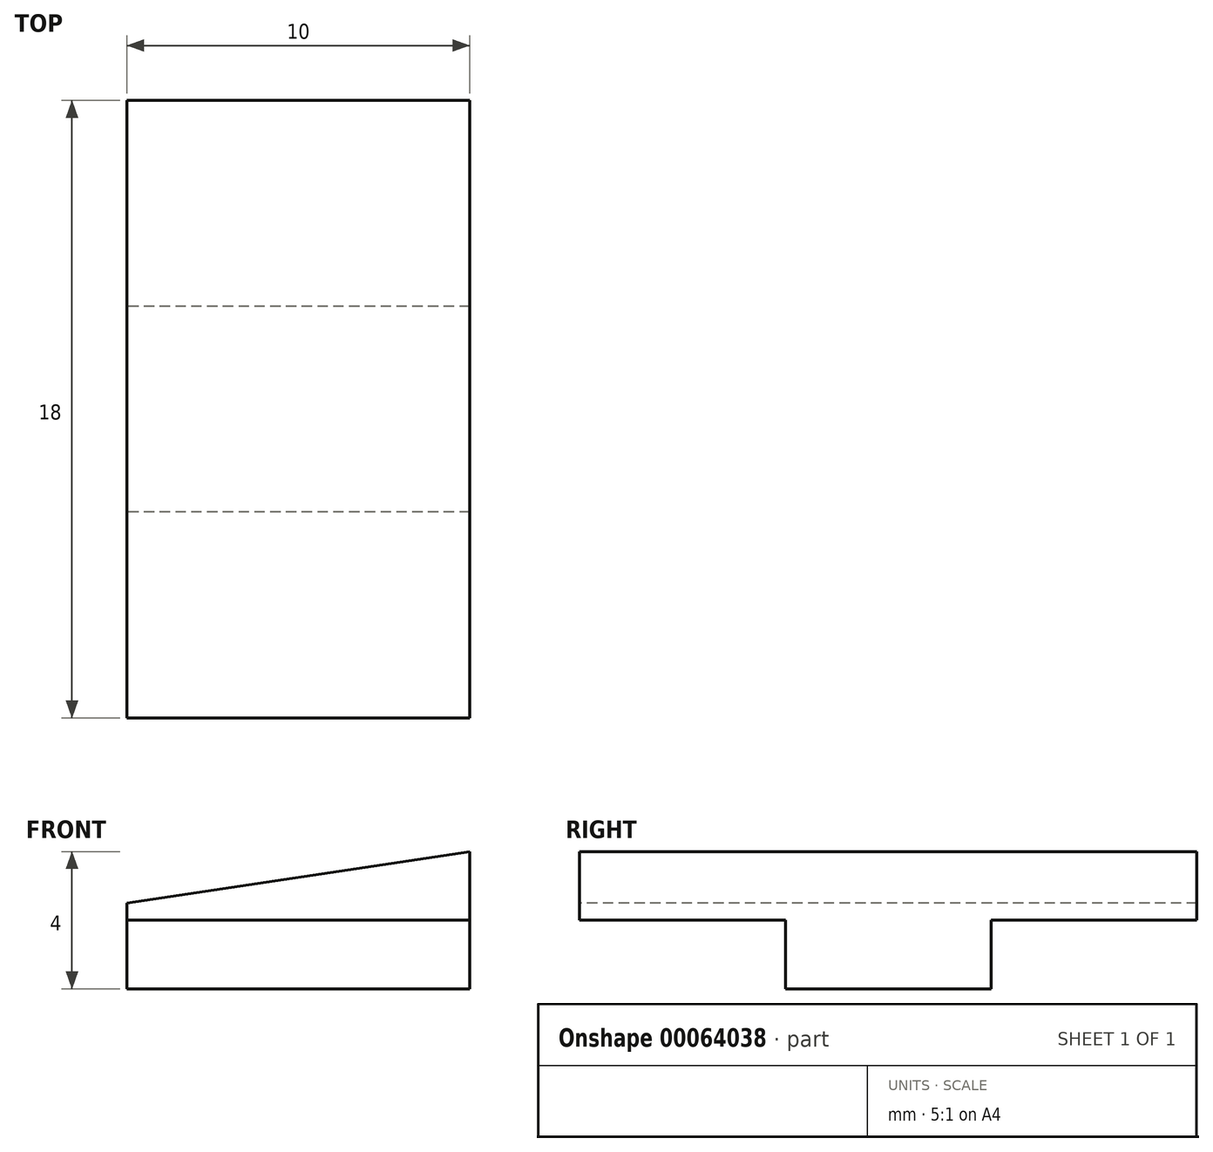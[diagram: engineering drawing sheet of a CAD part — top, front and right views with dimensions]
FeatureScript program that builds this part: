
annotation { "Feature Type Name" : "Feature", "Feature Type Description" : "" }
export const myFeature = defineFeature(function(context is Context, id is Id, definition is map)
    precondition{}
    {
        {
            var Q0;
            Q0=qCreatedBy(makeId("Top.planeOp"),FACE);
            var sketch = newSketch(context, id + "F0", { "sketchPlane" : qUnion([Q0])});
            skLineSegment(sketch, "E0.rect.bottom", {"start": v(5, -9) * mm, "end": v(-5, -9) * mm});
            skLineSegment(sketch, "E0.rect.top", {"start": v(5, 9) * mm, "end": v(-5, 9) * mm});
            skLineSegment(sketch, "E0.rect.left", {"start": v(5, -9) * mm, "end": v(5, 9) * mm});
            skLineSegment(sketch, "E0.rect.right", {"start": v(-5, -9) * mm, "end": v(-5, 9) * mm});
            skPoint(sketch, "E0.rect.middle", {"position": v(0, 0) * mm});
            skSolve(sketch);
        }
        {
            var Q0;
            Q0=makeQuery(id+"F0.imprint","IMPRINT",FACE,{"disambiguationData":[TD([[makeQuery(id+"F0.imprint","IMPRINT",EDGE,{"derivedFrom":sQuery(id+"F0.wireOp",EDGE,"E0.rect.bottom")}),-1.0]])]});
            extrude(context, id + "F1", {"entities" : qUnion([Q0]), "depth" : 4 * mm});
        }
        {
            var Q0;
            Q0=makeQuery(id+"F1.opExtrude","SWEPT_FACE",FACE,{"disambiguationData":[OSD([sQuery(id+"F0.wireOp",EDGE,"E0.rect.bottom")])]});
            var sketch = newSketch(context, id + "F2", { "sketchPlane" : qUnion([Q0])});
            skLineSegment(sketch, "E1", {"start": v(-5, 0.5) * mm, "end": v(5, 2) * mm});
            skLineSegment(sketch, "E2", {"start": v(-5, 0.5) * mm, "end": v(-5, 0) * mm});
            skLineSegment(sketch, "E3", {"start": v(-5, 0) * mm, "end": v(5, 0) * mm});
            skLineSegment(sketch, "E4", {"start": v(5, 0) * mm, "end": v(5, 2) * mm});
            skSolve(sketch);
        }
        {
            var Q0;
            Q0=makeQuery(id+"F2.imprint","IMPRINT",FACE,{"disambiguationData":[TD([[makeQuery(id+"F2.imprint","IMPRINT",EDGE,{"derivedFrom":sQuery(id+"F2.wireOp",EDGE,"E1")}),-1.0]])]});
            extrude(context, id + "F3", {"entities" : qUnion([Q0]), "operationType" : NewBodyOperationType.INTERSECT, "endBound" : BoundingType.THROUGH_ALL, "oppositeDirection" : true, "depth" : 25 * mm});
        }
        {
            var Q0;
            Q0=makeQuery(id+"F1.opExtrude","CAP_FACE",FACE,{"disambiguationData":[OSD([sQuery(id+"F0.wireOp",EDGE,"E0.rect.bottom"),sQuery(id+"F0.wireOp",EDGE,"E0.rect.top"),sQuery(id+"F0.wireOp",EDGE,"E0.rect.left"),sQuery(id+"F0.wireOp",EDGE,"E0.rect.right")])],"isStart":true});
            var sketch = newSketch(context, id + "F4", { "sketchPlane" : qUnion([Q0])});
            skLineSegment(sketch, "E5.rect.bottom", {"start": v(5, -3) * mm, "end": v(-5, -3) * mm});
            skLineSegment(sketch, "E5.rect.top", {"start": v(5, 3) * mm, "end": v(-5, 3) * mm});
            skLineSegment(sketch, "E5.rect.left", {"start": v(5, -3) * mm, "end": v(5, 3) * mm});
            skLineSegment(sketch, "E5.rect.right", {"start": v(-5, -3) * mm, "end": v(-5, 3) * mm});
            skPoint(sketch, "E5.rect.middle", {"position": v(0, 0) * mm});
            skSolve(sketch);
        }
        {
            var Q0;
            Q0 = qSketchRegion(id + "F4", true);
            extrude(context, id + "F5", {"entities" : qUnion([Q0]), "operationType" : NewBodyOperationType.ADD, "depth" : 2 * mm});
        }
    });
